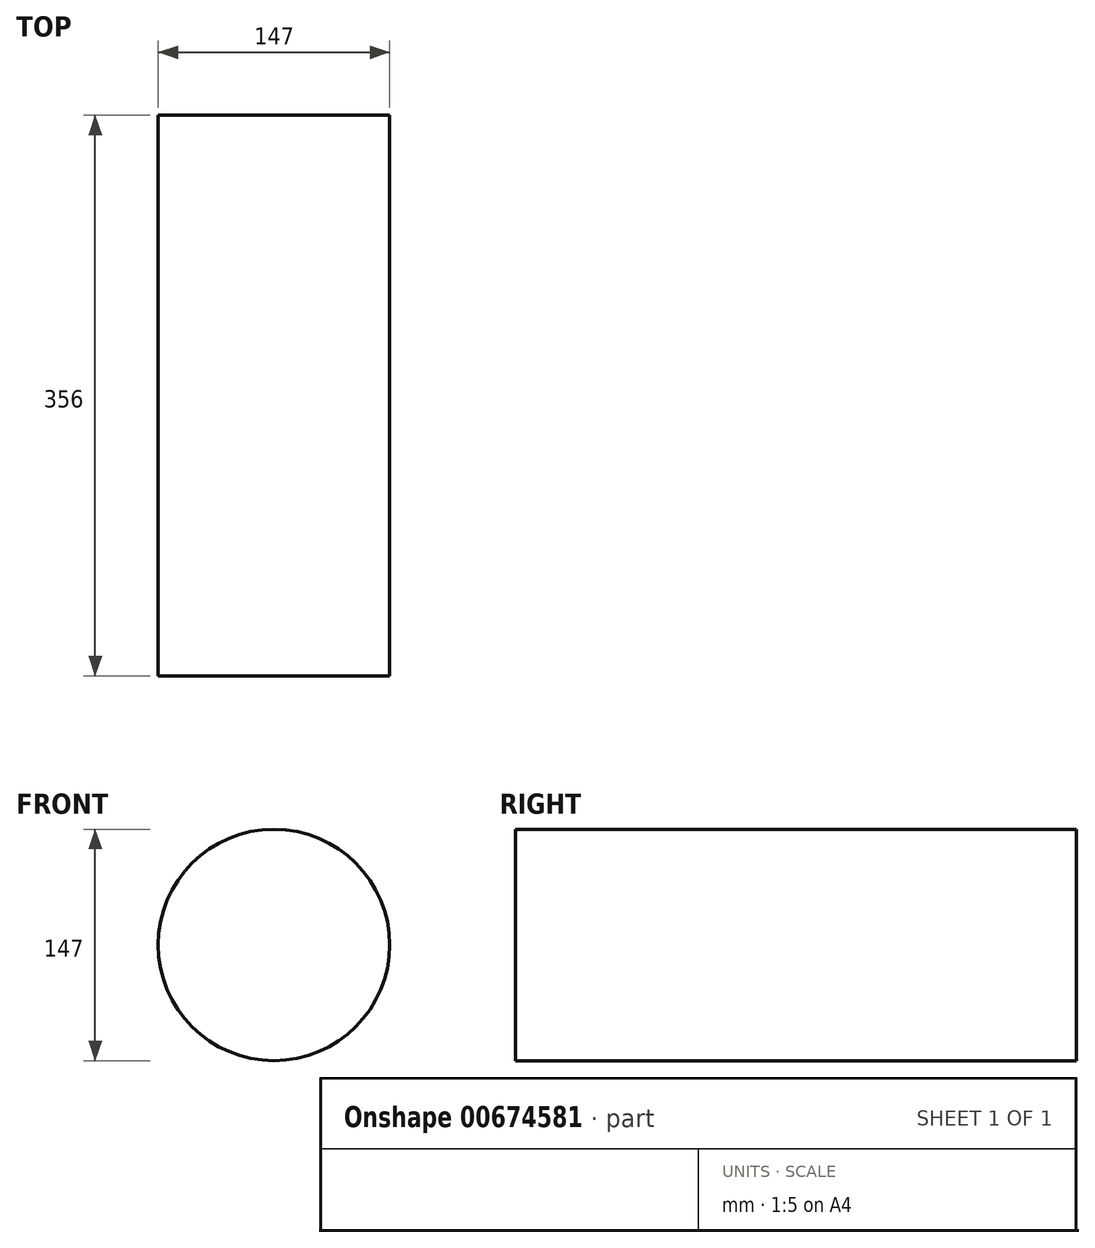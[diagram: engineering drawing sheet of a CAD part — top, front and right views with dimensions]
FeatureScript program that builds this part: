
annotation { "Feature Type Name" : "Feature", "Feature Type Description" : "" }
export const myFeature = defineFeature(function(context is Context, id is Id, definition is map)
    precondition{}
    {
        {
            var Q0;
            Q0=qCreatedBy(makeId("Front.planeOp"),FACE);
            var sketch = newSketch(context, id + "F0", { "sketchPlane" : qUnion([Q0])});
            skCircle(sketch, "E0", {"center": v(0, 0) * mm, "radius": 73.5 * mm});
            skSolve(sketch);
        }
        {
            var Q0;
            Q0=makeQuery(id+"F0.imprint","IMPRINT",FACE,{"disambiguationData":[TD([[makeQuery(id+"F0.imprint","IMPRINT",EDGE,{"derivedFrom":sQuery(id+"F0.wireOp",EDGE,"E0")}),1.0]])]});
            extrude(context, id + "F1", {"entities" : qUnion([Q0]), "depth" : 356 * mm, "offsetDistance" : 25 * mm});
        }
    });
